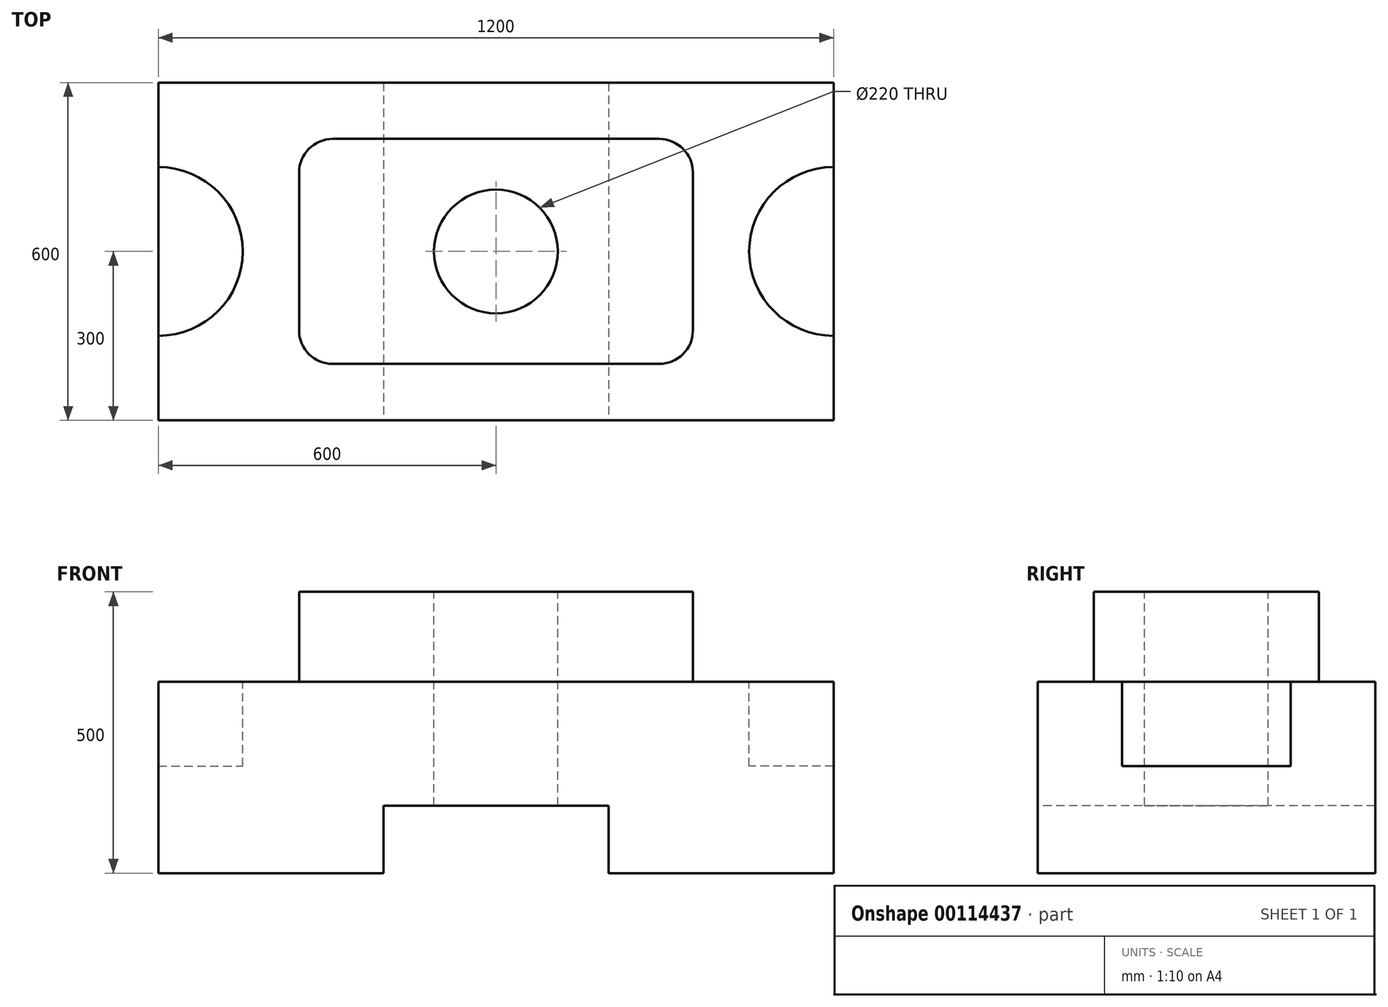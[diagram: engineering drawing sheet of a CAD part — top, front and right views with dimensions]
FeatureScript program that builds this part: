
annotation { "Feature Type Name" : "Feature", "Feature Type Description" : "" }
export const myFeature = defineFeature(function(context is Context, id is Id, definition is map)
    precondition{}
    {
        {
            var Q0;
            Q0=qCreatedBy(makeId("Top.planeOp"),FACE);
            var sketch = newSketch(context, id + "F0", { "sketchPlane" : qUnion([Q0])});
            skLineSegment(sketch, "E0.bottom", {"start": v(-600, -300) * mm, "end": v(600, -300) * mm});
            skLineSegment(sketch, "E0.top", {"start": v(-600, 300) * mm, "end": v(600, 300) * mm});
            skLineSegment(sketch, "E0.left", {"start": v(-600, -300) * mm, "end": v(-600, 300) * mm});
            skLineSegment(sketch, "E0.right", {"start": v(600, -300) * mm, "end": v(600, 300) * mm});
            skPoint(sketch, "E0.middle", {"position": v(0, 0) * mm});
            skSolve(sketch);
        }
        {
            var Q0;
            Q0 = qSketchRegion(id + "F0", true);
            extrude(context, id + "F1", {"entities" : qUnion([Q0]), "depth" : 340 * mm});
        }
        {
            var Q0;
            Q0=makeQuery(id+"F1.opExtrude","CAP_FACE",FACE,{"disambiguationData":[OSD([sQuery(id+"F0.wireOp",EDGE,"E0.bottom"),sQuery(id+"F0.wireOp",EDGE,"E0.top"),sQuery(id+"F0.wireOp",EDGE,"E0.left"),sQuery(id+"F0.wireOp",EDGE,"E0.right")])],"isStart":false});
            var sketch = newSketch(context, id + "F2", { "sketchPlane" : qUnion([Q0])});
            skCircle(sketch, "E1", {"center": v(-600, 0) * mm, "radius": 150 * mm});
            skCircle(sketch, "E2", {"center": v(600, 0) * mm, "radius": 150 * mm});
            skSolve(sketch);
        }
        {
            var Q0;
            {var subQ0=sQuery(id+"F2.wireOp",EDGE,"E1");var subQ1=makeQuery(id+"F1.opExtrude","CAP_EDGE",EDGE,{"disambiguationData":[OSD([sQuery(id+"F0.wireOp",EDGE,"E0.left")])],"isStart":false});var subQ2=makeQuery(id+"F2.imprint","INTERSECT",VERTEX,{"disambiguationData":[OD(0.0)],"derivedFrom":[subQ1,subQ0]});Q0=makeQuery(id+"F2.imprint","IMPRINT",FACE,{"disambiguationData":[TD([[makeQuery(id+"F2.imprint","IMPRINT",EDGE,{"disambiguationData":[TD([[subQ2,-1.0]])],"derivedFrom":subQ0}),1.0]])]});}
            var Q1;
            {var subQ0=sQuery(id+"F2.wireOp",EDGE,"E2");var subQ1=makeQuery(id+"F1.opExtrude","CAP_EDGE",EDGE,{"disambiguationData":[OSD([sQuery(id+"F0.wireOp",EDGE,"E0.right")])],"isStart":false});var subQ2=makeQuery(id+"F2.imprint","INTERSECT",VERTEX,{"disambiguationData":[OD(0.0)],"derivedFrom":[subQ1,subQ0]});Q1=makeQuery(id+"F2.imprint","IMPRINT",FACE,{"disambiguationData":[TD([[makeQuery(id+"F2.imprint","IMPRINT",EDGE,{"disambiguationData":[TD([[subQ2,1.0]])],"derivedFrom":subQ0}),1.0]])]});}
            var Q2;
            Q2=sQuery(id+"F2.wireOp",EDGE,"E1");
            var Q3;
            Q3=sQuery(id+"F2.wireOp",EDGE,"E2");
            extrude(context, id + "F3", {"entities" : qUnion([Q0, Q1]), "operationType" : NewBodyOperationType.REMOVE, "surfaceEntities" : qUnion([Q2, Q3]), "oppositeDirection" : true, "depth" : 150 * mm});
        }
        {
            var Q0;
            Q0=makeQuery(id+"F1.opExtrude","SWEPT_FACE",FACE,{"disambiguationData":[OSD([sQuery(id+"F0.wireOp",EDGE,"E0.bottom")])]});
            var sketch = newSketch(context, id + "F4", { "sketchPlane" : qUnion([Q0])});
            skLineSegment(sketch, "E3.bottom", {"start": v(200, 120) * mm, "end": v(-200, 120) * mm});
            skLineSegment(sketch, "E3.top", {"start": v(200, -120) * mm, "end": v(-200, -120) * mm});
            skLineSegment(sketch, "E3.left", {"start": v(200, 120) * mm, "end": v(200, -120) * mm});
            skLineSegment(sketch, "E3.right", {"start": v(-200, 120) * mm, "end": v(-200, -120) * mm});
            skPoint(sketch, "E3.middle", {"position": v(0, 0) * mm});
            skSolve(sketch);
        }
        {
            var Q0;
            Q0 = qSketchRegion(id + "F4", true);
            extrude(context, id + "F5", {"entities" : qUnion([Q0]), "operationType" : NewBodyOperationType.REMOVE, "endBound" : BoundingType.THROUGH_ALL, "oppositeDirection" : true, "depth" : 25 * mm});
        }
        {
            var Q0;
            Q0=makeQuery(id+"F1.opExtrude","CAP_FACE",FACE,{"disambiguationData":[OSD([sQuery(id+"F0.wireOp",EDGE,"E0.bottom"),sQuery(id+"F0.wireOp",EDGE,"E0.top"),sQuery(id+"F0.wireOp",EDGE,"E0.left"),sQuery(id+"F0.wireOp",EDGE,"E0.right")])],"isStart":false});
            var sketch = newSketch(context, id + "F6", { "sketchPlane" : qUnion([Q0])});
            skLineSegment(sketch, "E4.bottom", {"start": v(350, 200) * mm, "end": v(-350, 200) * mm});
            skLineSegment(sketch, "E4.top", {"start": v(350, -200) * mm, "end": v(-350, -200) * mm});
            skLineSegment(sketch, "E4.left", {"start": v(350, 200) * mm, "end": v(350, -200) * mm});
            skLineSegment(sketch, "E4.right", {"start": v(-350, 200) * mm, "end": v(-350, -200) * mm});
            skPoint(sketch, "E4.middle", {"position": v(0, 0) * mm});
            skSolve(sketch);
        }
        {
            var Q0;
            Q0 = qSketchRegion(id + "F6", true);
            extrude(context, id + "F7", {"entities" : qUnion([Q0]), "operationType" : NewBodyOperationType.ADD, "depth" : 160 * mm});
        }
        {
            var Q0;
            Q0=makeQuery(id+"F7.opExtrude","CAP_FACE",FACE,{"disambiguationData":[OSD([sQuery(id+"F6.wireOp",EDGE,"E4.bottom"),sQuery(id+"F6.wireOp",EDGE,"E4.top"),sQuery(id+"F6.wireOp",EDGE,"E4.left"),sQuery(id+"F6.wireOp",EDGE,"E4.right")])],"isStart":false});
            var sketch = newSketch(context, id + "F8", { "sketchPlane" : qUnion([Q0])});
            skCircle(sketch, "E5", {"center": v(0, 0) * mm, "radius": 110 * mm});
            skSolve(sketch);
        }
        {
            var Q0;
            Q0 = qSketchRegion(id + "F8", true);
            extrude(context, id + "F9", {"entities" : qUnion([Q0]), "operationType" : NewBodyOperationType.REMOVE, "endBound" : BoundingType.THROUGH_ALL, "oppositeDirection" : true, "depth" : 25 * mm});
        }
        {
            var Q0;
            Q0=makeQuery(id+"F7.opExtrude","SWEPT_EDGE",EDGE,{"disambiguationData":[OSD([sQuery(id+"F6.wireOp",EDGE,"E4.top"),sQuery(id+"F6.wireOp",EDGE,"E4.right")])]});
            var Q1;
            Q1=makeQuery(id+"F7.opExtrude","SWEPT_EDGE",EDGE,{"disambiguationData":[OSD([sQuery(id+"F6.wireOp",EDGE,"E4.bottom"),sQuery(id+"F6.wireOp",EDGE,"E4.right")])]});
            var Q2;
            Q2=makeQuery(id+"F7.opExtrude","SWEPT_EDGE",EDGE,{"disambiguationData":[OSD([sQuery(id+"F6.wireOp",EDGE,"E4.bottom"),sQuery(id+"F6.wireOp",EDGE,"E4.left")])]});
            var Q3;
            Q3=makeQuery(id+"F7.opExtrude","SWEPT_EDGE",EDGE,{"disambiguationData":[OSD([sQuery(id+"F6.wireOp",EDGE,"E4.top"),sQuery(id+"F6.wireOp",EDGE,"E4.left")])]});
            fillet(context, id + "F10", {"entities" : qUnion([Q0, Q1, Q2, Q3]), "radius" : 60 * mm, "tangentPropagation" : true, "allowEdgeOverflow" : false});
        }
    });
